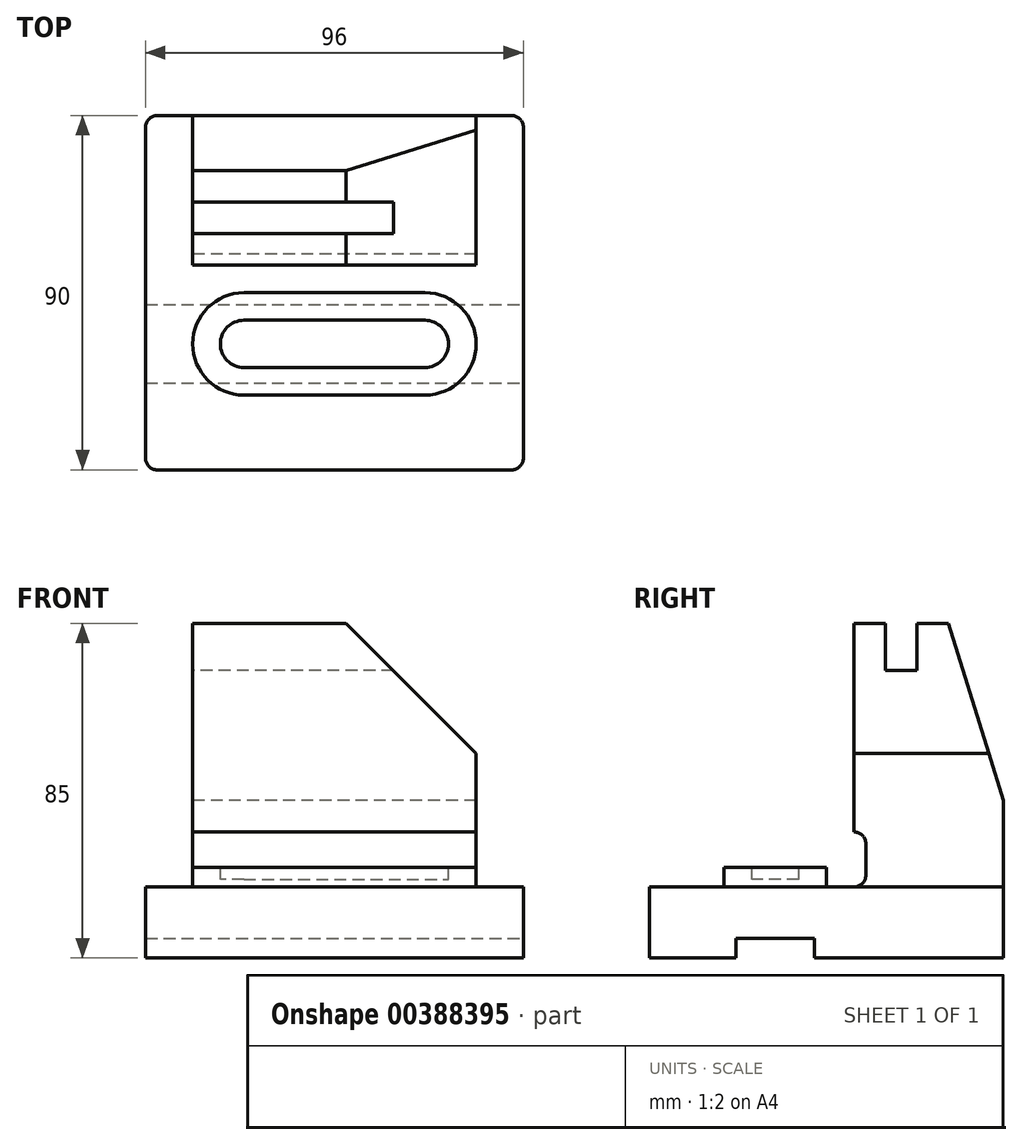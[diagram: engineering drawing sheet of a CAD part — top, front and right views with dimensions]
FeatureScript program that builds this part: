
annotation { "Feature Type Name" : "Feature", "Feature Type Description" : "" }
export const myFeature = defineFeature(function(context is Context, id is Id, definition is map)
    precondition{}
    {
        {
            var Q0;
            Q0=qCreatedBy(makeId("Top.planeOp"),FACE);
            var sketch = newSketch(context, id + "F0", { "sketchPlane" : qUnion([Q0])});
            skLineSegment(sketch, "E0.bottom", {"start": v(0, 0) * mm, "end": v(96, 0) * mm});
            skLineSegment(sketch, "E0.top", {"start": v(0, 90) * mm, "end": v(96, 90) * mm});
            skLineSegment(sketch, "E0.left", {"start": v(0, 0) * mm, "end": v(0, 90) * mm});
            skLineSegment(sketch, "E0.right", {"start": v(96, 0) * mm, "end": v(96, 90) * mm});
            skSolve(sketch);
        }
        {
            var Q0;
            Q0 = qSketchRegion(id + "F0", true);
            extrude(context, id + "F1", {"entities" : qUnion([Q0]), "depth" : 18 * mm});
        }
        {
            var Q0;
            Q0=makeQuery(id+"F1.opExtrude","CAP_FACE",FACE,{"disambiguationData":[OSD([sQuery(id+"F0.wireOp",EDGE,"E0.bottom"),sQuery(id+"F0.wireOp",EDGE,"E0.top"),sQuery(id+"F0.wireOp",EDGE,"E0.left"),sQuery(id+"F0.wireOp",EDGE,"E0.right")])],"isStart":false});
            var sketch = newSketch(context, id + "F2", { "sketchPlane" : qUnion([Q0])});
            skLineSegment(sketch, "E1.bottom", {"start": v(12, 90) * mm, "end": v(84, 90) * mm});
            skLineSegment(sketch, "E1.top", {"start": v(12, 52) * mm, "end": v(84, 52) * mm});
            skLineSegment(sketch, "E1.left", {"start": v(12, 90) * mm, "end": v(12, 52) * mm});
            skLineSegment(sketch, "E1.right", {"start": v(84, 90) * mm, "end": v(84, 52) * mm});
            skSolve(sketch);
        }
        {
            var Q0;
            Q0=makeQuery(id+"F1.opExtrude","CAP_FACE",FACE,{"disambiguationData":[OSD([sQuery(id+"F0.wireOp",EDGE,"E0.bottom"),sQuery(id+"F0.wireOp",EDGE,"E0.top"),sQuery(id+"F0.wireOp",EDGE,"E0.left"),sQuery(id+"F0.wireOp",EDGE,"E0.right")])],"isStart":true});
            cPlane(context, id + "F3", {"entities" : qUnion([Q0]), "cplaneType" : CPlaneType.OFFSET, "offset" : 85 * mm, "oppositeDirection" : true, "width" : 150 * mm, "height" : 150 * mm});
        }
        {
            var Q0;
            Q0 = qSketchRegion(id + "F2", true);
            var Q1;
            Q1=qCreatedBy(id+"F3.planeOp",FACE);
            extrude(context, id + "F4", {"entities" : qUnion([Q0]), "operationType" : NewBodyOperationType.ADD, "endBound" : BoundingType.UP_TO_SURFACE, "endBoundEntityFace" : qUnion([Q1]), "depth" : 58 * mm});
        }
        {
            var Q0;
            Q0=makeQuery(id+"F4.opExtrude","SWEPT_FACE",FACE,{"disambiguationData":[OSD([sQuery(id+"F2.wireOp",EDGE,"E1.top")])]});
            var sketch = newSketch(context, id + "F5", { "sketchPlane" : qUnion([Q0])});
            skLineSegment(sketch, "E2", {"start": v(84, 85) * mm, "end": v(51, 85) * mm});
            skLineSegment(sketch, "E3", {"start": v(51, 85) * mm, "end": v(84, 52) * mm});
            skSolve(sketch);
        }
        {
            var Q0;
            {var subQ0=sQuery(id+"F5.wireOp",EDGE,"E2");Q0=makeQuery(id+"F5.imprint","IMPRINT",FACE,{"disambiguationData":[TD([[makeQuery(id+"F5.imprint","IMPRINT",EDGE,{"derivedFrom":subQ0}),1.0]])]});}
            extrude(context, id + "F6", {"entities" : qUnion([Q0]), "operationType" : NewBodyOperationType.REMOVE, "oppositeDirection" : true, "depth" : 38 * mm});
        }
        {
            var Q0;
            Q0=makeQuery(id+"F4.opExtrude","SWEPT_FACE",FACE,{"disambiguationData":[OSD([sQuery(id+"F2.wireOp",EDGE,"E1.left")])]});
            var sketch = newSketch(context, id + "F7", { "sketchPlane" : qUnion([Q0])});
            skLineSegment(sketch, "E4.bottom", {"start": v(-68, 85) * mm, "end": v(-60, 85) * mm});
            skLineSegment(sketch, "E4.top", {"start": v(-68, 73) * mm, "end": v(-60, 73) * mm});
            skLineSegment(sketch, "E4.left", {"start": v(-68, 85) * mm, "end": v(-68, 73) * mm});
            skLineSegment(sketch, "E4.right", {"start": v(-60, 85) * mm, "end": v(-60, 73) * mm});
            skSolve(sketch);
        }
        {
            var Q0;
            Q0 = qSketchRegion(id + "F7", true);
            extrude(context, id + "F8", {"entities" : qUnion([Q0]), "operationType" : NewBodyOperationType.REMOVE, "endBound" : BoundingType.UP_TO_NEXT, "oppositeDirection" : true, "depth" : 25 * mm});
        }
        {
            var Q0;
            Q0=makeQuery(id+"F4.opExtrude","SWEPT_FACE",FACE,{"disambiguationData":[OSD([sQuery(id+"F2.wireOp",EDGE,"E1.left")])]});
            var sketch = newSketch(context, id + "F9", { "sketchPlane" : qUnion([Q0])});
            skLineSegment(sketch, "E5", {"start": v(-90, 85) * mm, "end": v(-76, 85) * mm});
            skLineSegment(sketch, "E6", {"start": v(-76, 85) * mm, "end": v(-90, 40) * mm});
            skSolve(sketch);
        }
        {
            var Q0;
            Q0 = qSketchRegion(id + "F9", true);
            var Q1;
            {var subQ0=sQuery(id+"F9.wireOp",EDGE,"E5");Q1=makeQuery(id+"F9.imprint","IMPRINT",FACE,{"disambiguationData":[TD([[makeQuery(id+"F9.imprint","IMPRINT",EDGE,{"derivedFrom":subQ0}),1.0]])]});}
            extrude(context, id + "F10", {"entities" : qUnion([Q0, Q1]), "operationType" : NewBodyOperationType.REMOVE, "endBound" : BoundingType.UP_TO_NEXT, "oppositeDirection" : true, "depth" : 25 * mm});
        }
        {
            var Q0;
            Q0=makeQuery(id+"F1.opExtrude","SWEPT_FACE",FACE,{"disambiguationData":[OSD([sQuery(id+"F0.wireOp",EDGE,"E0.right")])]});
            var sketch = newSketch(context, id + "F11", { "sketchPlane" : qUnion([Q0])});
            skLineSegment(sketch, "E7.bottom", {"start": v(42, 0) * mm, "end": v(22, 0) * mm});
            skLineSegment(sketch, "E7.top", {"start": v(42, 5) * mm, "end": v(22, 5) * mm});
            skLineSegment(sketch, "E7.left", {"start": v(42, 0) * mm, "end": v(42, 5) * mm});
            skLineSegment(sketch, "E7.right", {"start": v(22, 0) * mm, "end": v(22, 5) * mm});
            skPoint(sketch, "E8", {"position": v(32, 5) * mm});
            skSolve(sketch);
        }
        {
            var Q0;
            Q0 = qSketchRegion(id + "F11", true);
            extrude(context, id + "F12", {"entities" : qUnion([Q0]), "operationType" : NewBodyOperationType.REMOVE, "endBound" : BoundingType.UP_TO_NEXT, "oppositeDirection" : true, "depth" : 25 * mm});
        }
        {
            var Q0;
            Q0=makeQuery(id+"F4.opExtrude","SWEPT_EDGE",EDGE,{"disambiguationData":[OSD([sQuery(id+"F0.wireOp",EDGE,"E0.top"),sQuery(id+"F2.wireOp",EDGE,"E1.bottom"),sQuery(id+"F2.wireOp",EDGE,"E1.right")])]});
            var Q1;
            Q1=makeQuery(id+"F4.boolean.opBoolean","MERGE",FACE,{"derivedFrom":[makeQuery(id+"F1.opExtrude","SWEPT_FACE",FACE,{"disambiguationData":[OSD([sQuery(id+"F0.wireOp",EDGE,"E0.top")])]}),makeQuery(id+"F4.opExtrude","SWEPT_FACE",FACE,{"disambiguationData":[OSD([sQuery(id+"F2.wireOp",EDGE,"E1.bottom")])]})]});
            cPlane(context, id + "F13", {"entities" : qUnion([Q0, Q1]), "cplaneType" : CPlaneType.LINE_ANGLE, "offset" : 25 * mm, "angle" : 0 * degree, "width" : 150 * mm, "height" : 150 * mm});
        }
        {
            var Q0;
            Q0=makeQuery(id+"F1.opExtrude","CAP_FACE",FACE,{"disambiguationData":[OSD([sQuery(id+"F0.wireOp",EDGE,"E0.bottom"),sQuery(id+"F0.wireOp",EDGE,"E0.top"),sQuery(id+"F0.wireOp",EDGE,"E0.left"),sQuery(id+"F0.wireOp",EDGE,"E0.right")])],"isStart":false});
            var sketch = newSketch(context, id + "F14", { "sketchPlane" : qUnion([Q0])});
            skLineSegment(sketch, "E9.bottom", {"start": v(25, 45) * mm, "end": v(71, 45) * mm});
            skLineSegment(sketch, "E9.top", {"start": v(25, 19) * mm, "end": v(71, 19) * mm});
            skLineSegment(sketch, "E9.left", {"start": v(25, 45) * mm, "end": v(25, 19) * mm});
            skLineSegment(sketch, "E9.right", {"start": v(71, 45) * mm, "end": v(71, 19) * mm});
            skLineSegment(sketch, "E10", {"start": v(25, 32) * mm, "end": v(71, 32) * mm, "construction": true});
            skArc(sketch, "E11", {"start": v(71, 45) * mm, "mid": v(84, 32) * mm, "end": v(71, 19) * mm});
            skArc(sketch, "E12", {"start": v(25, 45) * mm, "mid": v(12, 32) * mm, "end": v(25, 19) * mm});
            skSolve(sketch);
        }
        {
            var Q0;
            Q0=makeQuery(id+"F14.imprint","IMPRINT",FACE,{"disambiguationData":[TD([[makeQuery(id+"F14.imprint","IMPRINT",EDGE,{"derivedFrom":sQuery(id+"F14.wireOp",EDGE,"E9.bottom")}),-1.0]])]});
            var Q1;
            Q1=makeQuery(id+"F14.imprint","IMPRINT",FACE,{"disambiguationData":[TD([[makeQuery(id+"F14.imprint","IMPRINT",EDGE,{"derivedFrom":sQuery(id+"F14.wireOp",EDGE,"E9.left")}),-1.0]])]});
            var Q2;
            Q2=makeQuery(id+"F14.imprint","IMPRINT",FACE,{"disambiguationData":[TD([[makeQuery(id+"F14.imprint","IMPRINT",EDGE,{"derivedFrom":sQuery(id+"F14.wireOp",EDGE,"E9.right")}),1.0]])]});
            extrude(context, id + "F15", {"entities" : qUnion([Q0, Q1, Q2]), "operationType" : NewBodyOperationType.ADD, "depth" : 5 * mm});
        }
        {
            var Q0;
            Q0=makeQuery(id+"F15.opExtrude","CAP_FACE",FACE,{"disambiguationData":[OSD([sQuery(id+"F14.wireOp",EDGE,"E9.bottom"),sQuery(id+"F14.wireOp",EDGE,"E9.top"),sQuery(id+"F14.wireOp",EDGE,"E11"),sQuery(id+"F14.wireOp",EDGE,"E12")])],"isStart":false});
            var sketch = newSketch(context, id + "F16", { "sketchPlane" : qUnion([Q0])});
            skLineSegment(sketch, "E13.JdR.JdR", {"start": v(25, 32) * mm, "end": v(71, 32) * mm, "construction": true});
            skArc(sketch, "E13.0.startCap", {"start": v(25, 26) * mm, "mid": v(19, 32) * mm, "end": v(25, 38) * mm});
            skArc(sketch, "E13.0.endCap", {"start": v(71, 38) * mm, "mid": v(77, 32) * mm, "end": v(71, 26) * mm});
            skLineSegment(sketch, "E13.0.left", {"start": v(25, 38) * mm, "end": v(71, 38) * mm});
            skLineSegment(sketch, "E13.0.right", {"start": v(25, 26) * mm, "end": v(71, 26) * mm});
            skSolve(sketch);
        }
        {
            var Q0;
            Q0 = qSketchRegion(id + "F16", true);
            extrude(context, id + "F17", {"entities" : qUnion([Q0]), "operationType" : NewBodyOperationType.REMOVE, "oppositeDirection" : true, "depth" : 3 * mm});
        }
        {
            var Q0;
            Q0=makeQuery(id+"F4.opExtrude","SWEPT_FACE",FACE,{"disambiguationData":[OSD([sQuery(id+"F2.wireOp",EDGE,"E1.right")])]});
            var sketch = newSketch(context, id + "F18", { "sketchPlane" : qUnion([Q0])});
            skLineSegment(sketch, "E14.bottom", {"start": v(52, 18) * mm, "end": v(55, 18) * mm});
            skLineSegment(sketch, "E14.top", {"start": v(52, 32) * mm, "end": v(55, 32) * mm});
            skLineSegment(sketch, "E14.left", {"start": v(52, 18) * mm, "end": v(52, 32) * mm});
            skLineSegment(sketch, "E14.right", {"start": v(55, 18) * mm, "end": v(55, 32) * mm});
            skSolve(sketch);
        }
        {
            var Q0;
            Q0=makeQuery(id+"F18.imprint","IMPRINT",FACE,{"disambiguationData":[TD([[makeQuery(id+"F18.imprint","IMPRINT",EDGE,{"derivedFrom":sQuery(id+"F18.wireOp",EDGE,"E14.bottom")}),-1.0]])]});
            extrude(context, id + "F19", {"entities" : qUnion([Q0]), "operationType" : NewBodyOperationType.REMOVE, "endBound" : BoundingType.UP_TO_NEXT, "oppositeDirection" : true, "depth" : 25 * mm});
        }
        {
            var Q0;
            Q0=makeQuery(id+"F15.opExtrude","CAP_EDGE",EDGE,{"disambiguationData":[OSD([sQuery(id+"F14.wireOp",EDGE,"E9.top")])],"isStart":true});
            var Q1;
            Q1=makeQuery(id+"F19.boolean.opBoolean","COPY",EDGE,{"derivedFrom":makeQuery(id+"F19.opExtrude","SWEPT_EDGE",EDGE,{"disambiguationData":[OSD([sQuery(id+"F2.wireOp",EDGE,"E1.right"),sQuery(id+"F18.wireOp",EDGE,"E14.bottom"),sQuery(id+"F18.wireOp",EDGE,"E14.right")])]})});
            var Q2;
            Q2=makeQuery(id+"F19.boolean.opBoolean","COPY",EDGE,{"derivedFrom":makeQuery(id+"F19.opExtrude","SWEPT_EDGE",EDGE,{"disambiguationData":[OSD([sQuery(id+"F18.wireOp",EDGE,"E14.top"),sQuery(id+"F18.wireOp",EDGE,"E14.right")])]})});
            var Q3;
            Q3=makeQuery(id+"F1.opExtrude","SWEPT_EDGE",EDGE,{"disambiguationData":[OSD([sQuery(id+"F0.wireOp",EDGE,"E0.bottom"),sQuery(id+"F0.wireOp",EDGE,"E0.left")])]});
            var Q4;
            Q4=makeQuery(id+"F1.opExtrude","SWEPT_EDGE",EDGE,{"disambiguationData":[OSD([sQuery(id+"F0.wireOp",EDGE,"E0.bottom"),sQuery(id+"F0.wireOp",EDGE,"E0.right")])]});
            var Q5;
            Q5=makeQuery(id+"F1.opExtrude","SWEPT_EDGE",EDGE,{"disambiguationData":[OSD([sQuery(id+"F0.wireOp",EDGE,"E0.top"),sQuery(id+"F0.wireOp",EDGE,"E0.right")])]});
            var Q6;
            Q6=makeQuery(id+"F1.opExtrude","SWEPT_EDGE",EDGE,{"disambiguationData":[OSD([sQuery(id+"F0.wireOp",EDGE,"E0.top"),sQuery(id+"F0.wireOp",EDGE,"E0.left")])]});
            var Q7;
            Q7=makeQuery(id+"F4.opExtrude","CAP_EDGE",EDGE,{"disambiguationData":[OSD([sQuery(id+"F2.wireOp",EDGE,"E1.right")])],"isStart":true});
            var Q8;
            Q8=makeQuery(id+"F4.opExtrude","CAP_EDGE",EDGE,{"disambiguationData":[OSD([sQuery(id+"F2.wireOp",EDGE,"E1.left")])],"isStart":true});
            fillet(context, id + "F20", {"entities" : qUnion([Q0, Q1, Q2, Q3, Q4, Q5, Q6, Q7, Q8]), "radius" : 3 * mm, "tangentPropagation" : true, "allowEdgeOverflow" : false});
        }
    });
